# Revit family: Sanitary-Equipment_Duravit_Urinal-Jim_085035
name_source: partatom
category: Plumbing Fixtures
revit_build: Autodesk Revit 2014 (Build: 20130308_1515(x64)
units: mm (PartAtom-declared; Revit-internal decimal feet)

## types (1)
- 085035 White Alpin
    BIMobject category = Urinals
    Depth (mm) = 350 mm  [stored 1.14829 ft]
    Description = Urinal visible inlet, syphonic action, vertical or horizontal outlet.
    Drain Diameter (mm) = 50 mm  [stored 0.164042 ft]
    Edition number = 1
    Height (mm) = 510 mm  [stored 1.67323 ft]
    IFC Classification = Sanitary Terminal
    Installation instructions = http://pro.duravit.com
    Manufacturer = Duravit
    Manufacturer name = DURAVIT
    Masterformat 2014 Code = 22 41 13.16
    Masterformat 2014 Description = Residential Urinals
    Model = 085035
    NBS Reference Code = 31-93
    NBS Reference Description = Urinal And Wc Fittings
    Nominal height = 0 mm  [stored 0 ft]
    Nominal width = 350 mm  [stored 1.14829 ft]
    OmniClass Code = 23-31 21 00
    OmniClass Description = Urinals
    Option 01 = Options : Model without fly
    Option 02 = Options : Model with fly
    Primary Material = Ceramics-Duravit-White_Alpin
    Product Guid = 3279a89d-e5f2-4aa7-a2b8-7d223ab35ad3
    Product SKU = urinals-urinal-jim-085035
    Product certification = http://pro.duravit.com
    Product data url = https://bimobject.com
    Product family = Urinals
    Product group = Urinal Jim
    QR code = http://bimobject.com
    Specification = 08503500071: Urinal Jim white visible inlet, with fly, WG 0850350000: Urinal Jim white visible inlet 08503500001: Urinal Jim white visible inlet, WonderGliss 0850350007: Urinal Jim white visible inlet, with fly 0850352800: 0850355200: 0850355600:
    Technical description = http://pro.duravit.com
    UNSPSC Code = 30181506
    URL = http://www.duravit.de
    Uniclass 1.4 Code = L721
    Uniclass 1.4 Description = Sanitary equipment
    Uniclass 2.0 Code = PR-31-93
    Uniclass 2.0 Description = Urinal And Wc Fittings
    Uniclass 2015 Code = Pr_40_20_93
    Uniclass 2015 Name = Urinal and WC fittings
    Uniformat II Code = D2010
    Uniformat II Description = Plumbing Fixtures
    Water Inlet Diameter (mm) = 35 mm  [stored 0.114829 ft]
    Weight Net (Kg) = 12
    Width (mm) = 360 mm  [stored 1.1811 ft]

note: [stored X ft] marks values corroborated as IEEE doubles in the binary element streams (Revit-internal decimal feet)

## geometry (parser evidence)
native form markers: Sweep x5
no freeform markers — native parametric forms only
